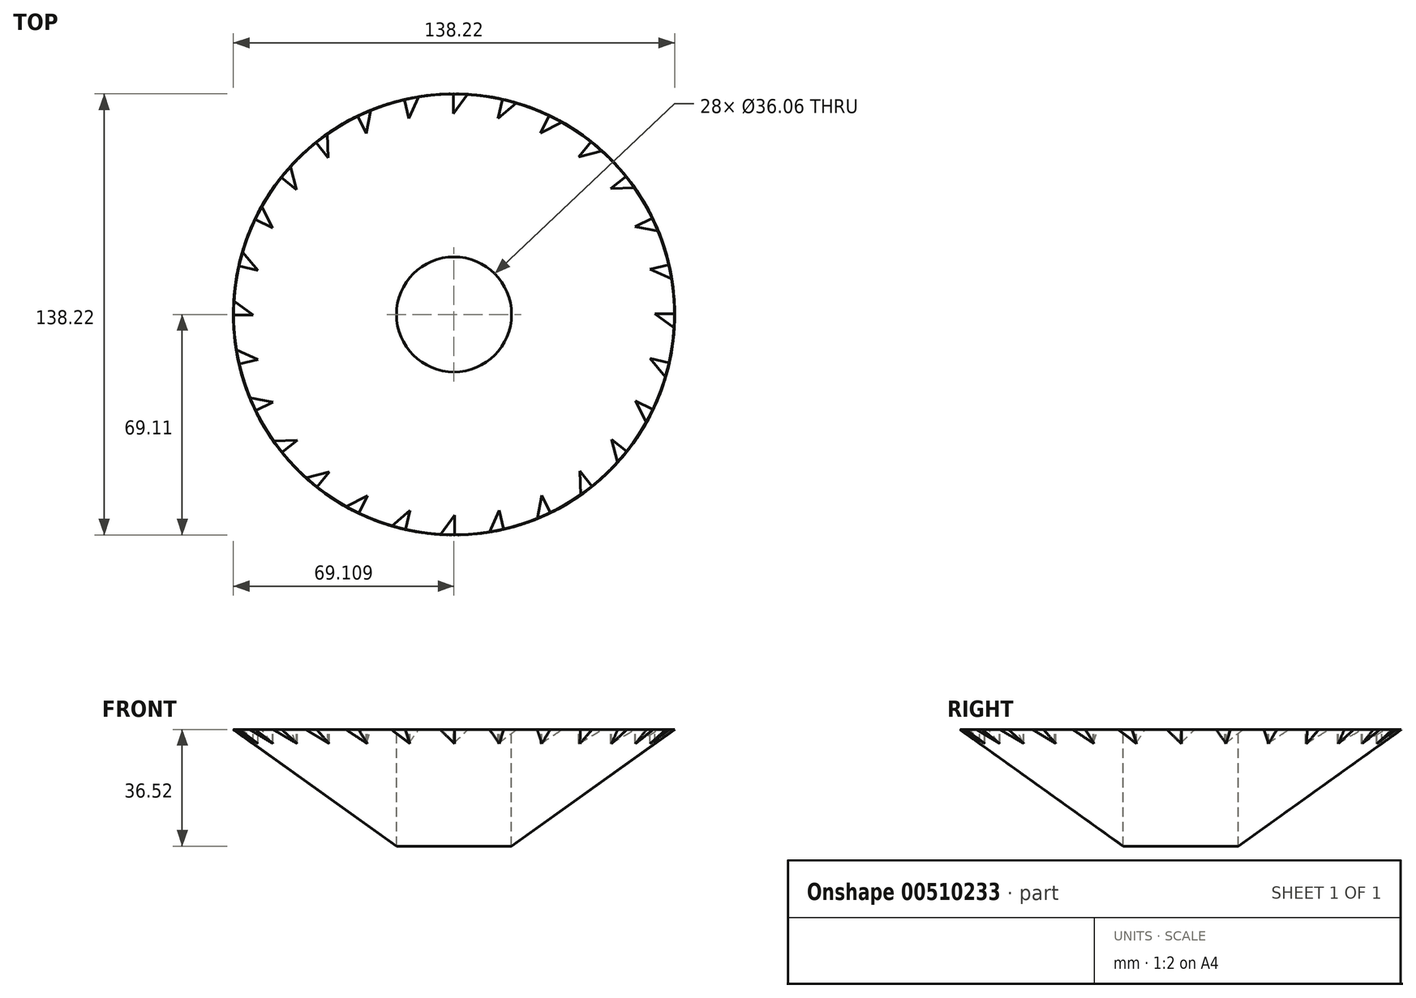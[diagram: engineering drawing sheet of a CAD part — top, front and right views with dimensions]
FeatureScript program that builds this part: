
annotation { "Feature Type Name" : "Feature", "Feature Type Description" : "" }
export const myFeature = defineFeature(function(context is Context, id is Id, definition is map)
    precondition{}
    {
        {
            var Q0;
            Q0=qCreatedBy(makeId("Front.planeOp"),FACE);
            var sketch = newSketch(context, id + "F0", { "sketchPlane" : qUnion([Q0])});
            skLineSegment(sketch, "E0", {"start": v(0, 0) * mm, "end": v(-51.08, 36.52) * mm});
            skLineSegment(sketch, "E1", {"start": v(-51.08, 36.52) * mm, "end": v(0, 36.52) * mm});
            skLineSegment(sketch, "E2", {"start": v(0, 36.52) * mm, "end": v(0, 10.17) * mm});
            skLineSegment(sketch, "E3", {"start": v(0, 10.17) * mm, "end": v(18.03, 10.17) * mm});
            skLineSegment(sketch, "E4", {"start": v(18.03, 10.17) * mm, "end": v(18.03, 0) * mm});
            skLineSegment(sketch, "E5", {"start": v(18.03, 0) * mm, "end": v(0, 0) * mm});
            skSolve(sketch);
        }
        {
            var Q0;
            Q0=makeQuery(id+"F0.imprint","IMPRINT",FACE,{"disambiguationData":[TD([[makeQuery(id+"F0.imprint","IMPRINT",EDGE,{"derivedFrom":sQuery(id+"F0.wireOp",EDGE,"E0")}),-1.0]])]});
            var Q1;
            Q1=sQuery(id+"F0.wireOp",EDGE,"E4");
            revolve(context, id + "F1", {"entities" : qUnion([Q0]), "axis" : qUnion([Q1]), "revolveType" : RevolveType.FULL});
        }
        {
            var Q0;
            Q0=makeQuery(id+"F1.opRevolve","SWEPT_FACE",FACE,{"disambiguationData":[OSD([sQuery(id+"F0.wireOp",EDGE,"E3")])]});
            extrude(context, id + "F2", {"entities" : qUnion([Q0]), "operationType" : NewBodyOperationType.REMOVE, "oppositeDirection" : true, "depth" : 30 * mm});
        }
        {
            var Q0;
            Q0=makeQuery(id+"F1.opRevolve","SWEPT_FACE",FACE,{"disambiguationData":[OSD([sQuery(id+"F0.wireOp",EDGE,"E1")])]});
            var sketch = newSketch(context, id + "F3", { "sketchPlane" : qUnion([Q0])});
            skLineSegment(sketch, "E6", {"start": v(17.84, 73.5) * mm, "end": v(17.84, 62.97) * mm});
            skLineSegment(sketch, "E7", {"start": v(17.84, 62.97) * mm, "end": v(24.6, 71.99) * mm});
            skLineSegment(sketch, "E8", {"start": v(24.6, 71.99) * mm, "end": v(17.84, 73.5) * mm});
            skSolve(sketch);
        }
        {
            var Q0;
            {var subQ0=sQuery(id+"F3.wireOp",EDGE,"E7");var subQ1=sQuery(id+"F3.wireOp",EDGE,"E6");var subQ2=makeQuery(id+"F3.imprint","INTERSECT",VERTEX,{"derivedFrom":[subQ1,subQ0]});Q0=makeQuery(id+"F3.imprint","IMPRINT",FACE,{"disambiguationData":[TD([[makeQuery(id+"F3.imprint","IMPRINT",EDGE,{"disambiguationData":[TD([[subQ2,1.0]])],"derivedFrom":subQ1}),1.0]])]});}
            extrude(context, id + "F4", {"entities" : qUnion([Q0]), "operationType" : NewBodyOperationType.REMOVE, "oppositeDirection" : true, "depth" : 25 * mm});
        }
        {
            var Q0;
            Q0=makeQuery(id+"F1.opRevolve","SWEPT_BODY",BODY,{"disambiguationData":[OSD([sQuery(id+"F0.wireOp",EDGE,"E0"),sQuery(id+"F0.wireOp",EDGE,"E1"),sQuery(id+"F0.wireOp",EDGE,"E2"),sQuery(id+"F0.wireOp",EDGE,"E3"),sQuery(id+"F0.wireOp",EDGE,"E4"),sQuery(id+"F0.wireOp",EDGE,"E5")])]});
            var Q1;
            Q1=makeQuery(id+"F1.opRevolve","SWEPT_EDGE",EDGE,{"disambiguationData":[OSD([sQuery(id+"F0.wireOp",EDGE,"E1"),sQuery(id+"F0.wireOp",EDGE,"E2")])]});
            circularPattern(context, id + "F5", {"entities" : qUnion([Q0]), "axis" : qUnion([Q1]), "angle" : 360 * degree, "instanceCount" : 28, "equalSpace" : true});
        }
    });
